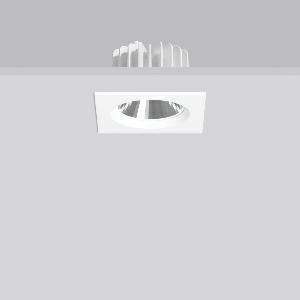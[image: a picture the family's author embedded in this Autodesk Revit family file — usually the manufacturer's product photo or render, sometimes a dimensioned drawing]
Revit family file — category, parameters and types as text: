
# Revit family: ledona_square_ip20_901531_002_2_76_cada
name_source: partatom
category: Lighting Fixtures
units: mm (PartAtom-declared; Revit-internal decimal feet)

## family parameters
Cut with Voids When Loaded = No
Host = Face
Light Source = No
Part Type = Normal
Room Calculation Point = No
Round Connector Dimension = Use Diameter
Shared = No

## types (1)
- TuneableWhite 846 (1 x LED Modul 846, 1350 lm, 4600)
    Apparent Load = 16 VA
    CIE Flux Codes = 94 100 100 100 100
    Color Rendering = 80
    Color Temperature = 4600
    Default Elevation = 1800 mm
    Description = Series: LEDONA square
Recessed LED downlight featuring advanced technology and sophisticated design. Housing: die-cast aluminium constructed as heat sink. Square cover plate: die-cast aluminium, powder coated. Round ceiling cut-out also with square types. Tunable white dynamically adjustable from 2700 K to 6500 K. Installation without tools thanks to spring fastening system. With connected DALI DT8 driver in separate box. With connecting cable (L 250 mm). Through-wiring box (5 pole) available as accessory. 
Colour: white
Length: 130 mm
Width: 130 mm
Height: 3 mm
Cut-out diameter: 120 mm
Recess height: 105 mm
Luminaire: recess height: 79 mm
Lamp: LED
Socket: without socket
Colour temperature: 2700K - 6500K
Colour rendering index (CRI): 80
System power: 16 W
Rated luminous flux: 1350 lm
Luminous efficiency: 84 lm/W
System power 2: 16 W
Rated luminous flux 2: 1400 lm
Luminous efficiency 2: 88 lm/W
System power 3: 17 W
Rated luminous flux 3: 1300 lm
Luminous efficiency 3: 76 lm/W
Control gear: Converter, dimmable, DALI
Protection class: II
Type of protection: IP 20
    Height = 0 mm  [stored 0 ft]
    Lamp = 1 x LED Modul 846
    Lamp Light Flux = 1350 lm
    Lamp count = 1
    Length = 130 mm
    Lifetime = 50000 h
    Luminous efficacy = 84 lm/W
    Manufacturer = RZB
    ModVariant = No
    Model = 901531.002.2.76
    Mounting Place = Ceiling
    Mounting Type = Recessed
    Number of Poles = 1
    OnlyDefault = Yes
    Power Factor = 1
    Product Name = LEDONA square IP20
    Product group = Recessed downlights
    ProductGroupID = 402
    Protection Class = Protection class II
    Protection Degree = IP 20
    RLX_Detail_Level = 1
    RLX_Emergency_Light_Flux = 0 lm
    RLX_Emergency_Type = 0
    RLX_Emergency_Type_DB = No
    RlxData = <blob elided: 30977 chars, md5=40779653>
    Socket = socket
    Standby Power = 0 W
    System Light Flux = 1350 lm
    System Power = 16 W
    Type Comments = TuneableWhite 846
    Type Image = 901389.002.jpg
    URL = http://relux.com
    VarID = tuneablewhite_846
    Voltage = 230 V
    Voltage Range = 220-240 V
    Weight = 0.00 kg
    Width = 130 mm

note: [stored X ft] marks values corroborated as IEEE doubles in the binary element streams (Revit-internal decimal feet)

## geometry (parser evidence)
native form markers: Blend x4, Sweep x9
no freeform markers — native parametric forms only
